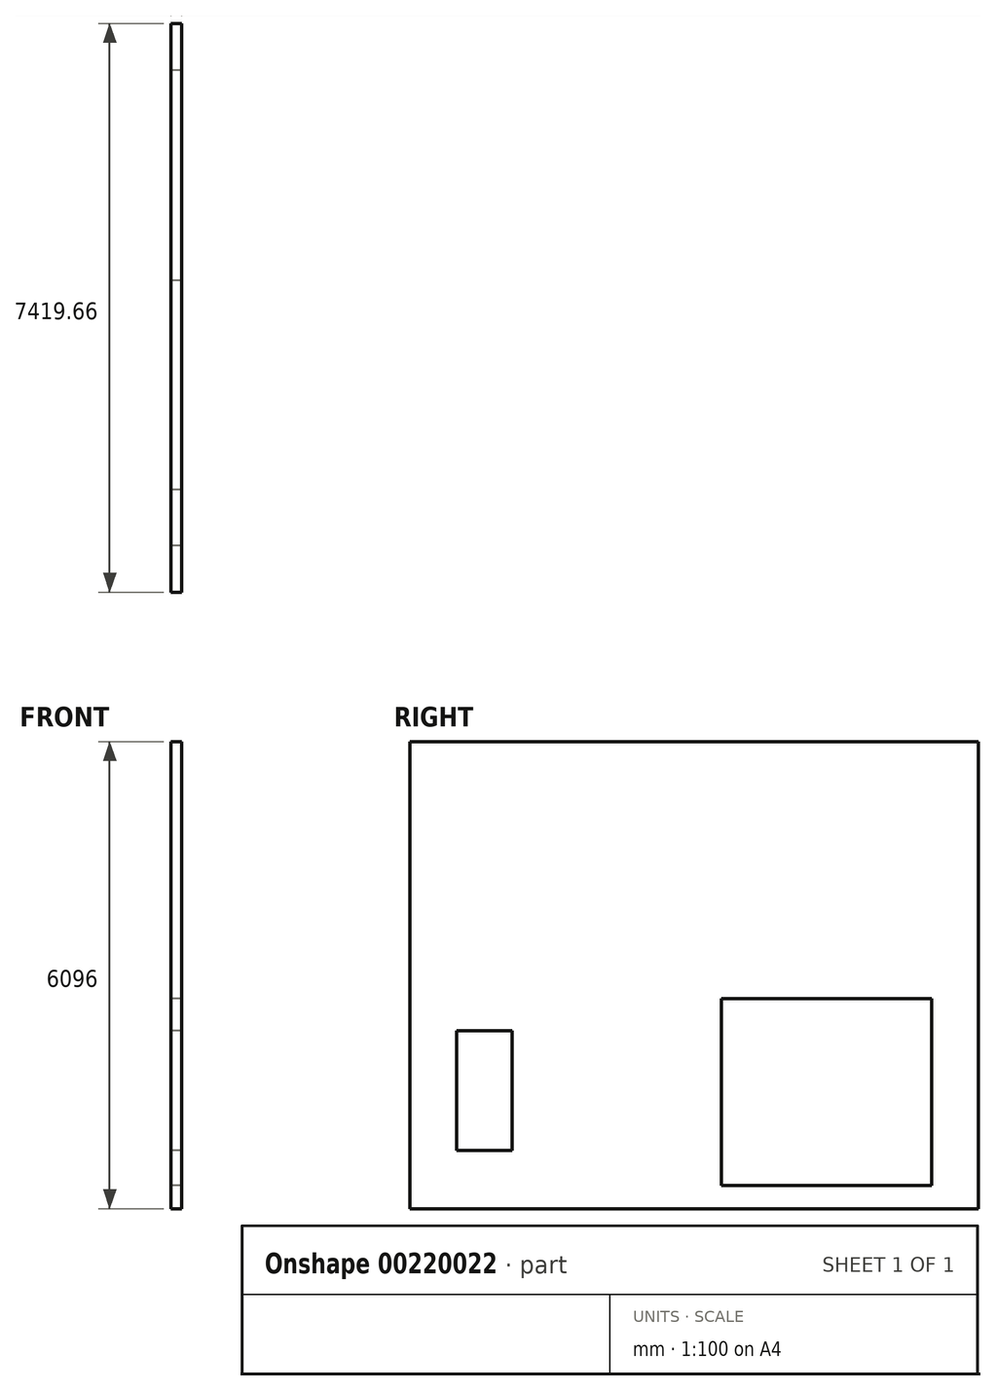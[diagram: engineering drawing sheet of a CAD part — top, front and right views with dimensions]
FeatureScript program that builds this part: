
annotation { "Feature Type Name" : "Feature", "Feature Type Description" : "" }
export const myFeature = defineFeature(function(context is Context, id is Id, definition is map)
    precondition{}
    {
        {
            var Q0;
            Q0=qCreatedBy(makeId("Right.planeOp"),FACE);
            var sketch = newSketch(context, id + "F0", { "sketchPlane" : qUnion([Q0])});
            skLineSegment(sketch, "E0.bottom", {"start": v(0, 0) * mm, "end": v(7419.66, 0) * mm});
            skLineSegment(sketch, "E0.top", {"start": v(0, 6096) * mm, "end": v(7419.66, 6096) * mm});
            skLineSegment(sketch, "E0.left", {"start": v(0, 0) * mm, "end": v(0, 6096) * mm});
            skLineSegment(sketch, "E0.right", {"start": v(7419.66, 0) * mm, "end": v(7419.66, 6096) * mm});
            skSolve(sketch);
        }
        {
            var Q0;
            Q0=makeQuery(id+"F0.imprint","IMPRINT",FACE,{"disambiguationData":[TD([[makeQuery(id+"F0.imprint","IMPRINT",EDGE,{"derivedFrom":sQuery(id+"F0.wireOp",EDGE,"E0.bottom")}),1.0]])]});
            extrude(context, id + "F1", {"entities" : qUnion([Q0]), "depth" : 138.27 * mm});
        }
        {
            var Q0;
            Q0=qCreatedBy(makeId("Front.planeOp"),FACE);
            var sketch = newSketch(context, id + "F2", { "sketchPlane" : qUnion([Q0])});
            skLineSegment(sketch, "E1", {"start": v(0, 6096) * mm, "end": v(2933.7, 10515.6) * mm, "construction": true});
            skLineSegment(sketch, "E2", {"start": v(0, 6096) * mm, "end": v(-609.6, 5177.64) * mm, "construction": true});
            skSolve(sketch);
        }
        {
            var Q0;
            Q0=sQuery(id+"F2.wireOp",VERTEX,"E2.end");
            var Q1;
            Q1=makeQuery(id+"F1.opExtrude","CAP_FACE",FACE,{"disambiguationData":[OSD([sQuery(id+"F0.wireOp",EDGE,"E0.bottom"),sQuery(id+"F0.wireOp",EDGE,"E0.top"),sQuery(id+"F0.wireOp",EDGE,"E0.left"),sQuery(id+"F0.wireOp",EDGE,"E0.right")])],"isStart":true});
            cPlane(context, id + "F3", {"entities" : qUnion([Q0, Q1]), "cplaneType" : CPlaneType.PLANE_POINT, "offset" : 25.4 * mm, "width" : 152.4 * mm, "height" : 152.4 * mm});
        }
        {
            var Q0;
            Q0=makeQuery(id+"F1.opExtrude","CAP_FACE",FACE,{"disambiguationData":[OSD([sQuery(id+"F0.wireOp",EDGE,"E0.bottom"),sQuery(id+"F0.wireOp",EDGE,"E0.top"),sQuery(id+"F0.wireOp",EDGE,"E0.left"),sQuery(id+"F0.wireOp",EDGE,"E0.right")])],"isStart":true});
            var sketch = newSketch(context, id + "F4", { "sketchPlane" : qUnion([Q0])});
            skLineSegment(sketch, "E3.bottom", {"start": v(-1335.25, 2321.7) * mm, "end": v(-609.6, 2321.7) * mm});
            skLineSegment(sketch, "E3.top", {"start": v(-1335.25, 762) * mm, "end": v(-609.6, 762) * mm});
            skLineSegment(sketch, "E3.left", {"start": v(-1335.25, 2321.7) * mm, "end": v(-1335.25, 762) * mm});
            skLineSegment(sketch, "E3.right", {"start": v(-609.6, 2321.7) * mm, "end": v(-609.6, 762) * mm});
            skLineSegment(sketch, "E4.bottom", {"start": v(-6810.06, 304.8) * mm, "end": v(-4066.86, 304.8) * mm});
            skLineSegment(sketch, "E4.top", {"start": v(-6810.06, 2743.2) * mm, "end": v(-4066.86, 2743.2) * mm});
            skLineSegment(sketch, "E4.left", {"start": v(-6810.06, 304.8) * mm, "end": v(-6810.06, 2743.2) * mm});
            skLineSegment(sketch, "E4.right", {"start": v(-4066.86, 304.8) * mm, "end": v(-4066.86, 2743.2) * mm});
            skSolve(sketch);
        }
        {
            var Q0;
            Q0=makeQuery(id+"F4.imprint","IMPRINT",FACE,{"disambiguationData":[TD([[makeQuery(id+"F4.imprint","IMPRINT",EDGE,{"derivedFrom":sQuery(id+"F4.wireOp",EDGE,"E4.bottom")}),1.0]])]});
            var Q1;
            Q1=makeQuery(id+"F4.imprint","IMPRINT",FACE,{"disambiguationData":[TD([[makeQuery(id+"F4.imprint","IMPRINT",EDGE,{"derivedFrom":sQuery(id+"F4.wireOp",EDGE,"E3.bottom")}),-1.0]])]});
            extrude(context, id + "F5", {"entities" : qUnion([Q0, Q1]), "operationType" : NewBodyOperationType.REMOVE, "endBound" : BoundingType.THROUGH_ALL, "oppositeDirection" : true, "depth" : 25.4 * mm});
        }
    });
